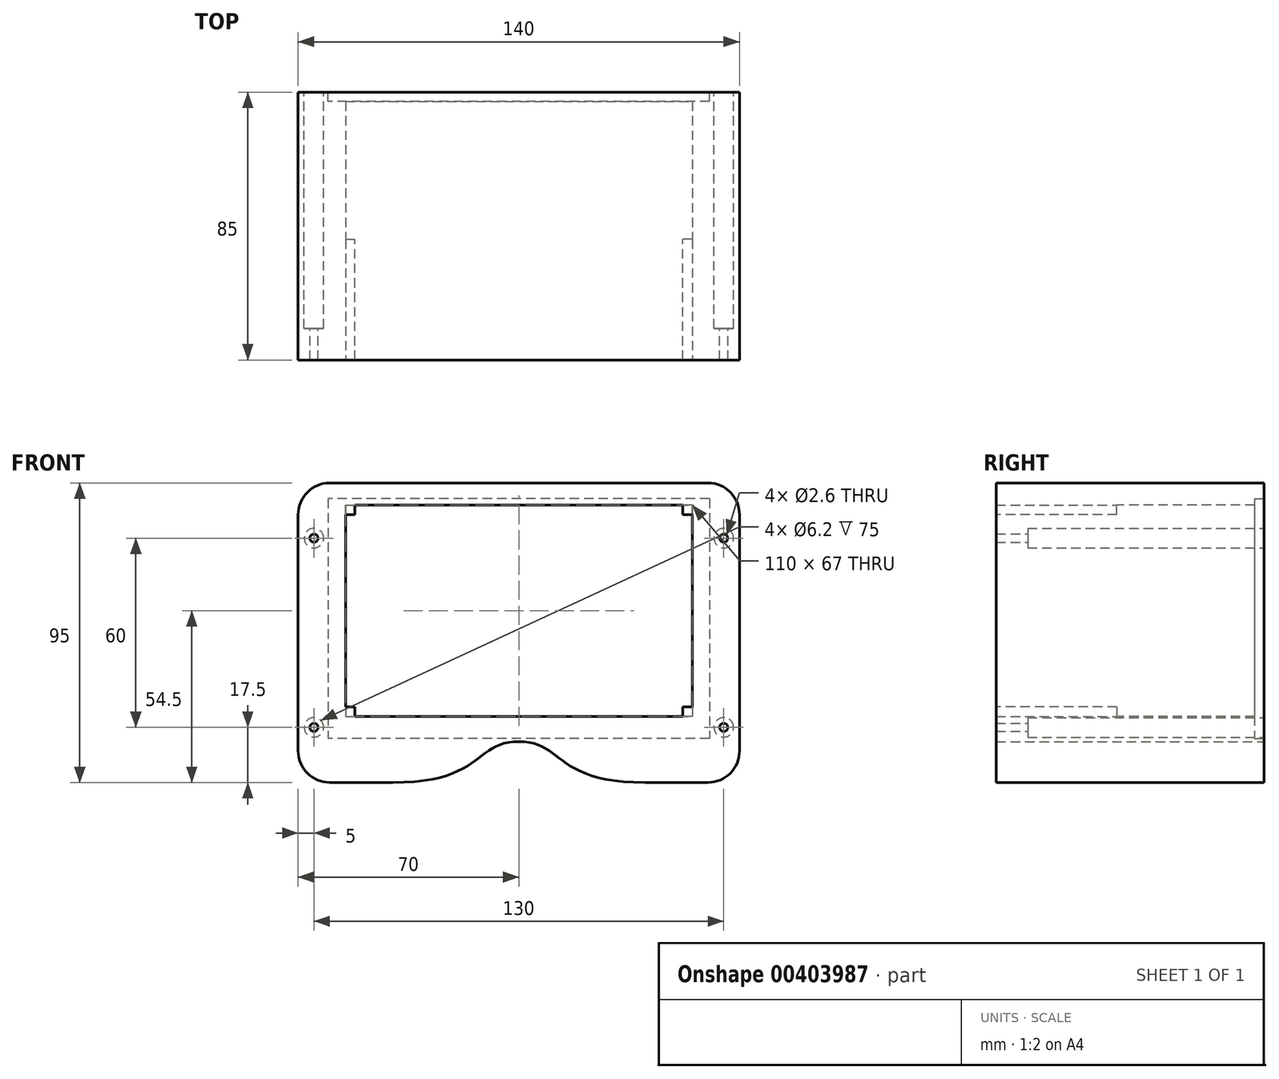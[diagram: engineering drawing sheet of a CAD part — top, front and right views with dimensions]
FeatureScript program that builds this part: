
annotation { "Feature Type Name" : "Feature", "Feature Type Description" : "" }
export const myFeature = defineFeature(function(context is Context, id is Id, definition is map)
    precondition{}
    {
        {
            var Q0;
            Q0=qCreatedBy(makeId("Top.planeOp"),FACE);
            var sketch = newSketch(context, id + "F0", { "sketchPlane" : qUnion([Q0])});
            skLineSegment(sketch, "E0.bottom", {"start": v(70, 85) * mm, "end": v(-70, 85) * mm});
            skLineSegment(sketch, "E0.top", {"start": v(70, -85) * mm, "end": v(-70, -85) * mm});
            skLineSegment(sketch, "E0.left", {"start": v(70, 85) * mm, "end": v(70, -85) * mm});
            skLineSegment(sketch, "E0.right", {"start": v(-70, 85) * mm, "end": v(-70, -85) * mm});
            skPoint(sketch, "E0.middle", {"position": v(0, 0) * mm});
            skSolve(sketch);
        }
        {
            var Q0;
            Q0=qSketchRegion(id+"F0",true);
            extrude(context, id + "F1", {"entities" : qUnion([Q0]), "depth" : 95 * mm});
        }
        {
            var Q0;
            Q0=makeQuery(id+"F1.opExtrude","SWEPT_FACE",FACE,{"disambiguationData":[OSD([sQuery(id+"F0.wireOp",EDGE,"E0.top")])]});
            var sketch = newSketch(context, id + "F2", { "sketchPlane" : qUnion([Q0])});
            skLineSegment(sketch, "E1.bottom", {"start": v(-55, 88) * mm, "end": v(55, 88) * mm});
            skLineSegment(sketch, "E1.top", {"start": v(-55, 21) * mm, "end": v(55, 21) * mm});
            skLineSegment(sketch, "E1.left", {"start": v(-55, 88) * mm, "end": v(-55, 21) * mm});
            skLineSegment(sketch, "E1.right", {"start": v(55, 88) * mm, "end": v(55, 21) * mm});
            skSolve(sketch);
        }
        {
            var Q0;
            Q0=qSketchRegion(id+"F2",true);
            extrude(context, id + "F3", {"entities" : qUnion([Q0]), "operationType" : NewBodyOperationType.REMOVE, "endBound" : BoundingType.THROUGH_ALL, "oppositeDirection" : true, "depth" : 25 * mm});
        }
        {
            var Q0;
            Q0=makeQuery(id+"F1.opExtrude","CAP_FACE",FACE,{"disambiguationData":[OSD([sQuery(id+"F0.wireOp",EDGE,"E0.bottom"),sQuery(id+"F0.wireOp",EDGE,"E0.top"),sQuery(id+"F0.wireOp",EDGE,"E0.left"),sQuery(id+"F0.wireOp",EDGE,"E0.right")])],"isStart":true});
            var sketch = newSketch(context, id + "F4", { "sketchPlane" : qUnion([Q0])});
            skLineSegment(sketch, "E2", {"start": v(0, -85) * mm, "end": v(0, 85) * mm, "construction": true});
            skLineSegment(sketch, "E3.1.0.0", {"start": v(-10, -85) * mm, "end": v(-10, 85) * mm, "construction": true});
            skLineSegment(sketch, "E3.2.0.0", {"start": v(-20, -85) * mm, "end": v(-20, 85) * mm, "construction": true});
            skLineSegment(sketch, "E3.3.0.0", {"start": v(-30, -85) * mm, "end": v(-30, 85) * mm, "construction": true});
            skLineSegment(sketch, "E3.4.0.0", {"start": v(-40, -85) * mm, "end": v(-40, 85) * mm, "construction": true});
            skLineSegment(sketch, "E3.5.0.0", {"start": v(-50, -85) * mm, "end": v(-50, 85) * mm, "construction": true});
            skLineSegment(sketch, "E3.6.0.0", {"start": v(-60, -85) * mm, "end": v(-60, 85) * mm, "construction": true});
            skLineSegment(sketch, "E3.direction1", {"start": v(0, -85) * mm, "end": v(-10, -85) * mm, "construction": true});
            skLineSegment(sketch, "E4.1.0.0", {"start": v(10, -85) * mm, "end": v(10, 85) * mm, "construction": true});
            skLineSegment(sketch, "E4.2.0.0", {"start": v(20, -85) * mm, "end": v(20, 85) * mm, "construction": true});
            skLineSegment(sketch, "E4.3.0.0", {"start": v(30, -85) * mm, "end": v(30, 85) * mm, "construction": true});
            skLineSegment(sketch, "E4.4.0.0", {"start": v(40, -85) * mm, "end": v(40, 85) * mm, "construction": true});
            skLineSegment(sketch, "E4.5.0.0", {"start": v(50, -85) * mm, "end": v(50, 85) * mm, "construction": true});
            skLineSegment(sketch, "E4.6.0.0", {"start": v(60, -85) * mm, "end": v(60, 85) * mm, "construction": true});
            skLineSegment(sketch, "E4.direction1", {"start": v(0, -85) * mm, "end": v(10, -85) * mm, "construction": true});
            skLineSegment(sketch, "E5", {"start": v(70, 15) * mm, "end": v(-70, 15) * mm, "construction": true});
            skLineSegment(sketch, "E6.0.1.0", {"start": v(70, 25) * mm, "end": v(-70, 25) * mm, "construction": true});
            skLineSegment(sketch, "E6.0.2.0", {"start": v(70, 35) * mm, "end": v(-70, 35) * mm, "construction": true});
            skLineSegment(sketch, "E6.0.3.0", {"start": v(70, 45) * mm, "end": v(-70, 45) * mm, "construction": true});
            skLineSegment(sketch, "E6.0.4.0", {"start": v(70, 55) * mm, "end": v(-70, 55) * mm, "construction": true});
            skLineSegment(sketch, "E6.0.5.0", {"start": v(70, 65) * mm, "end": v(-70, 65) * mm, "construction": true});
            skLineSegment(sketch, "E6.0.6.0", {"start": v(70, 75) * mm, "end": v(-70, 75) * mm, "construction": true});
            skLineSegment(sketch, "E6.1.0.0", {"start": v(95, 15) * mm, "end": v(-45, 15) * mm, "construction": true});
            skLineSegment(sketch, "E6.1.1.0", {"start": v(95, 25) * mm, "end": v(-45, 25) * mm, "construction": true});
            skLineSegment(sketch, "E6.1.2.0", {"start": v(95, 35) * mm, "end": v(-45, 35) * mm, "construction": true});
            skLineSegment(sketch, "E6.1.3.0", {"start": v(95, 45) * mm, "end": v(-45, 45) * mm, "construction": true});
            skLineSegment(sketch, "E6.1.4.0", {"start": v(95, 55) * mm, "end": v(-45, 55) * mm, "construction": true});
            skLineSegment(sketch, "E6.1.5.0", {"start": v(95, 65) * mm, "end": v(-45, 65) * mm, "construction": true});
            skLineSegment(sketch, "E6.1.6.0", {"start": v(95, 75) * mm, "end": v(-45, 75) * mm, "construction": true});
            skLineSegment(sketch, "E6.2.0.0", {"start": v(120, 15) * mm, "end": v(-20, 15) * mm, "construction": true});
            skLineSegment(sketch, "E6.2.1.0", {"start": v(120, 25) * mm, "end": v(-20, 25) * mm, "construction": true});
            skLineSegment(sketch, "E6.2.2.0", {"start": v(120, 35) * mm, "end": v(-20, 35) * mm, "construction": true});
            skLineSegment(sketch, "E6.2.3.0", {"start": v(120, 45) * mm, "end": v(-20, 45) * mm, "construction": true});
            skLineSegment(sketch, "E6.2.4.0", {"start": v(120, 55) * mm, "end": v(-20, 55) * mm, "construction": true});
            skLineSegment(sketch, "E6.2.5.0", {"start": v(120, 65) * mm, "end": v(-20, 65) * mm, "construction": true});
            skLineSegment(sketch, "E6.2.6.0", {"start": v(120, 75) * mm, "end": v(-20, 75) * mm, "construction": true});
            skLineSegment(sketch, "E6.direction1", {"start": v(-70, 15) * mm, "end": v(-45, 15) * mm, "construction": true});
            skLineSegment(sketch, "E6.direction2", {"start": v(-70, 15) * mm, "end": v(-70, 25) * mm, "construction": true});
            skFitSpline(sketch, "E7", {"points": [v(0, 15) * mm, v(20, 45) * mm, v(31.85, 56.6) * mm, v(68.26, 85) * mm], "startDerivative": vector(65.7, 0) * mm, "endDerivative": vector(77.5, 177.86) * mm});
            skFitSpline(sketch, "E8.MirrorCS", {"points": [v(0, 15) * mm, v(-20, 45) * mm, v(-31.85, 56.6) * mm, v(-68.26, 85) * mm], "startDerivative": vector(-65.7, 0) * mm, "endDerivative": vector(-77.5, 177.86) * mm});
            skLineSegment(sketch, "E9", {"start": v(68.26, 85) * mm, "end": v(-68.26, 85) * mm});
            skSolve(sketch);
        }
        {
            var Q0;
            Q0=makeQuery(id+"F4.imprint","IMPRINT",FACE,{"disambiguationData":[TD([[makeQuery(id+"F4.imprint","IMPRINT",EDGE,{"derivedFrom":sQuery(id+"F4.wireOp",EDGE,"E7")}),1.0]])]});
            extrude(context, id + "F5", {"entities" : qUnion([Q0]), "operationType" : NewBodyOperationType.REMOVE, "oppositeDirection" : true, "depth" : 88 * mm});
        }
        {
            var Q0;
            Q0=makeQuery(id+"F1.opExtrude","CAP_FACE",FACE,{"disambiguationData":[OSD([sQuery(id+"F0.wireOp",EDGE,"E0.bottom"),sQuery(id+"F0.wireOp",EDGE,"E0.top"),sQuery(id+"F0.wireOp",EDGE,"E0.left"),sQuery(id+"F0.wireOp",EDGE,"E0.right")])],"isStart":false});
            var sketch = newSketch(context, id + "F6", { "sketchPlane" : qUnion([Q0])});
            skLineSegment(sketch, "E10", {"start": v(-70, -55) * mm, "end": v(70, -55) * mm, "construction": true});
            skLineSegment(sketch, "E11", {"start": v(68.3, -85) * mm, "end": v(68.3, -55) * mm, "construction": true});
            skLineSegment(sketch, "E12", {"start": v(-68.36, -85) * mm, "end": v(-68.36, -55) * mm, "construction": true});
            skLineSegment(sketch, "E13", {"start": v(0, -85) * mm, "end": v(0, -55) * mm, "construction": true});
            skFitSpline(sketch, "E14", {"points": [v(0, -55) * mm, v(-47.97, -64.27) * mm, v(-68.36, -85) * mm], "startDerivative": vector(-134.93, 0) * mm, "endDerivative": vector(-37.97, -66.04) * mm});
            skFitSpline(sketch, "E15.MirrorCS", {"points": [v(0, -55) * mm, v(47.97, -64.27) * mm, v(68.36, -85) * mm], "startDerivative": vector(134.93, 0) * mm, "endDerivative": vector(37.97, -66.04) * mm});
            skLineSegment(sketch, "E16", {"start": v(-68.36, -85) * mm, "end": v(68.36, -85) * mm});
            skSolve(sketch);
        }
        {
            var Q0;
            Q0=makeQuery(id+"F6.imprint","IMPRINT",FACE,{"disambiguationData":[TD([[makeQuery(id+"F6.imprint","IMPRINT",EDGE,{"derivedFrom":sQuery(id+"F6.wireOp",EDGE,"E14")}),1.0]])]});
            extrude(context, id + "F7", {"entities" : qUnion([Q0]), "operationType" : NewBodyOperationType.REMOVE, "endBound" : BoundingType.UP_TO_NEXT, "oppositeDirection" : true, "depth" : 25 * mm});
        }
        {
            var Q0;
            Q0=makeQuery(id+"F1.opExtrude","CAP_EDGE",EDGE,{"disambiguationData":[OSD([sQuery(id+"F0.wireOp",EDGE,"E0.left")])],"isStart":false});
            var Q1;
            Q1=makeQuery(id+"F1.opExtrude","CAP_EDGE",EDGE,{"disambiguationData":[OSD([sQuery(id+"F0.wireOp",EDGE,"E0.left")])],"isStart":true});
            var Q2;
            Q2=makeQuery(id+"F1.opExtrude","CAP_EDGE",EDGE,{"disambiguationData":[OSD([sQuery(id+"F0.wireOp",EDGE,"E0.right")])],"isStart":true});
            var Q3;
            Q3=makeQuery(id+"F1.opExtrude","CAP_EDGE",EDGE,{"disambiguationData":[OSD([sQuery(id+"F0.wireOp",EDGE,"E0.right")])],"isStart":false});
            fillet(context, id + "F8", {"entities" : qUnion([Q0, Q1, Q2, Q3]), "radius" : 10 * mm, "tangentPropagation" : true, "allowEdgeOverflow" : false});
        }
        {
            var Q0;
            Q0=makeQuery(id+"F1.opExtrude","SWEPT_FACE",FACE,{"disambiguationData":[OSD([sQuery(id+"F0.wireOp",EDGE,"E0.bottom")])]});
            var sketch = newSketch(context, id + "F9", { "sketchPlane" : qUnion([Q0])});
            skLineSegment(sketch, "E17", {"start": v(0, 21) * mm, "end": v(0, 0) * mm, "construction": true});
            skLineSegment(sketch, "E18", {"start": v(-70, 13) * mm, "end": v(70, 13) * mm, "construction": true});
            skLineSegment(sketch, "E19", {"start": v(-40, 21) * mm, "end": v(-40, 0) * mm, "construction": true});
            skFitSpline(sketch, "E20", {"points": [v(0, 13) * mm, v(-40, 0) * mm], "startDerivative": vector(-42.54, 0) * mm, "endDerivative": vector(-86.95, 0) * mm});
            skFitSpline(sketch, "E21.MirrorCS", {"points": [v(0, 13) * mm, v(40, 0) * mm], "startDerivative": vector(42.54, 0) * mm, "endDerivative": vector(86.95, 0) * mm});
            skLineSegment(sketch, "E22", {"start": v(40, 0) * mm, "end": v(-40, 0) * mm});
            skSolve(sketch);
        }
        {
            var Q0;
            Q0=makeQuery(id+"F9.imprint","IMPRINT",FACE,{"disambiguationData":[TD([[makeQuery(id+"F9.imprint","IMPRINT",EDGE,{"derivedFrom":sQuery(id+"F9.wireOp",EDGE,"E20")}),1.0]])]});
            extrude(context, id + "F10", {"entities" : qUnion([Q0]), "operationType" : NewBodyOperationType.REMOVE, "endBound" : BoundingType.THROUGH_ALL, "oppositeDirection" : true, "depth" : 25 * mm});
        }
        {
            var Q0;
            Q0=makeQuery(id+"F1.opExtrude","SWEPT_FACE",FACE,{"disambiguationData":[OSD([sQuery(id+"F0.wireOp",EDGE,"E0.bottom")])]});
            var sketch = newSketch(context, id + "F11", { "sketchPlane" : qUnion([Q0])});
            skLineSegment(sketch, "E23.bottom", {"start": v(-60.5, 90) * mm, "end": v(60.5, 90) * mm});
            skLineSegment(sketch, "E23.top", {"start": v(-60.5, 14) * mm, "end": v(60.5, 14) * mm});
            skLineSegment(sketch, "E23.left", {"start": v(-60.5, 90) * mm, "end": v(-60.5, 14) * mm});
            skLineSegment(sketch, "E23.right", {"start": v(60.5, 90) * mm, "end": v(60.5, 14) * mm});
            skSolve(sketch);
        }
        {
            var Q0;
            Q0=makeQuery(id+"F11.imprint","IMPRINT",FACE,{"disambiguationData":[TD([[makeQuery(id+"F11.imprint","IMPRINT",EDGE,{"derivedFrom":sQuery(id+"F11.wireOp",EDGE,"E23.bottom")}),-1.0]])]});
            extrude(context, id + "F12", {"entities" : qUnion([Q0]), "operationType" : NewBodyOperationType.REMOVE, "oppositeDirection" : true, "depth" : 3 * mm});
        }
        {
            var Q0;
            Q0=makeQuery(id+"F3.boolean.opBoolean","COPY",FACE,{"derivedFrom":makeQuery(id+"F3.opExtrude","SWEPT_FACE",FACE,{"disambiguationData":[OSD([sQuery(id+"F2.wireOp",EDGE,"E1.top")])]})});
            var sketch = newSketch(context, id + "F13", { "sketchPlane" : qUnion([Q0])});
            skLineSegment(sketch, "E24.bottom", {"start": v(-55, -51.7) * mm, "end": v(-52, -51.7) * mm});
            skLineSegment(sketch, "E24.top", {"start": v(-55, 38.3) * mm, "end": v(-52, 38.3) * mm});
            skLineSegment(sketch, "E24.left", {"start": v(-55, -51.7) * mm, "end": v(-55, 38.3) * mm});
            skLineSegment(sketch, "E24.right", {"start": v(-52, -51.7) * mm, "end": v(-52, 38.3) * mm});
            skLineSegment(sketch, "E25.bottom", {"start": v(55, -51.7) * mm, "end": v(52, -51.7) * mm});
            skLineSegment(sketch, "E25.top", {"start": v(55, 38.3) * mm, "end": v(52, 38.3) * mm});
            skLineSegment(sketch, "E25.left", {"start": v(55, -51.7) * mm, "end": v(55, 38.3) * mm});
            skLineSegment(sketch, "E25.right", {"start": v(52, -51.7) * mm, "end": v(52, 38.3) * mm});
            skSolve(sketch);
        }
        {
            var Q0;
            Q0=qSketchRegion(id+"F13",true);
            extrude(context, id + "F14", {"entities" : qUnion([Q0]), "operationType" : NewBodyOperationType.ADD, "depth" : 3 * mm});
        }
        {
            var Q0;
            Q0=makeQuery(id+"F5.boolean.opBoolean","MERGE",FACE,{"derivedFrom":[makeQuery(id+"F3.boolean.opBoolean","COPY",FACE,{"derivedFrom":makeQuery(id+"F3.opExtrude","SWEPT_FACE",FACE,{"disambiguationData":[OSD([sQuery(id+"F2.wireOp",EDGE,"E1.bottom")])]})}),makeQuery(id+"F5.opExtrude","CAP_FACE",FACE,{"disambiguationData":[OSD([sQuery(id+"F4.wireOp",EDGE,"E7"),sQuery(id+"F4.wireOp",EDGE,"E8.MirrorCS"),sQuery(id+"F4.wireOp",EDGE,"E9")])],"isStart":false})]});
            var sketch = newSketch(context, id + "F15", { "sketchPlane" : qUnion([Q0])});
            skLineSegment(sketch, "E26.bottom", {"start": v(55, 51.7) * mm, "end": v(52, 51.7) * mm});
            skLineSegment(sketch, "E26.top", {"start": v(55, -38.3) * mm, "end": v(52, -38.3) * mm});
            skLineSegment(sketch, "E26.left", {"start": v(55, 51.7) * mm, "end": v(55, -38.3) * mm});
            skLineSegment(sketch, "E26.right", {"start": v(52, 51.7) * mm, "end": v(52, -38.3) * mm});
            skLineSegment(sketch, "E27.bottom", {"start": v(-55, 51.7) * mm, "end": v(-52, 51.7) * mm});
            skLineSegment(sketch, "E27.top", {"start": v(-55, -38.3) * mm, "end": v(-52, -38.3) * mm});
            skLineSegment(sketch, "E27.left", {"start": v(-55, 51.7) * mm, "end": v(-55, -38.3) * mm});
            skLineSegment(sketch, "E27.right", {"start": v(-52, 51.7) * mm, "end": v(-52, -38.3) * mm});
            skSolve(sketch);
        }
        {
            var Q0;
            Q0=qSketchRegion(id+"F15",true);
            extrude(context, id + "F16", {"entities" : qUnion([Q0]), "operationType" : NewBodyOperationType.ADD, "depth" : 3 * mm});
        }
        {
            var Q0;
            Q0=makeQuery(id+"F1.opExtrude","SWEPT_FACE",FACE,{"disambiguationData":[OSD([sQuery(id+"F0.wireOp",EDGE,"E0.bottom")])]});
            var sketch = newSketch(context, id + "F17", { "sketchPlane" : qUnion([Q0])});
            skLineSegment(sketch, "E28", {"start": v(-70, 47.5) * mm, "end": v(70, 47.5) * mm, "construction": true});
            skCircle(sketch, "E29", {"center": v(65, 77.5) * mm, "radius": 1.3 * mm});
            skLineSegment(sketch, "E30", {"start": v(0, 95) * mm, "end": v(0, 13) * mm, "construction": true});
            skCircle(sketch, "E31.MirrorC", {"center": v(65, 17.5) * mm, "radius": 1.3 * mm});
            skCircle(sketch, "E32.MirrorC", {"center": v(-65, 77.5) * mm, "radius": 1.3 * mm});
            skCircle(sketch, "E33.MirrorC", {"center": v(-65, 17.5) * mm, "radius": 1.3 * mm});
            skSolve(sketch);
        }
        {
            var Q0;
            Q0=qSketchRegion(id+"F17",true);
            extrude(context, id + "F18", {"entities" : qUnion([Q0]), "operationType" : NewBodyOperationType.REMOVE, "oppositeDirection" : true, "depth" : 100 * mm});
        }
        {
            var Q0;
            Q0=makeQuery(id+"F17.imprint","IMPRINT",FACE,{"disambiguationData":[TD([[makeQuery(id+"F17.imprint","IMPRINT",EDGE,{"derivedFrom":sQuery(id+"F17.wireOp",EDGE,"E29")}),-1.0]])]});
            var sketch = newSketch(context, id + "F19", { "sketchPlane" : qUnion([Q0])});
            skCircle(sketch, "E34", {"center": v(65, 77.5) * mm, "radius": 3.1 * mm});
            skCircle(sketch, "E35.MirrorC", {"center": v(65, 17.5) * mm, "radius": 3.1 * mm});
            skCircle(sketch, "E36.MirrorC", {"center": v(-65, 77.5) * mm, "radius": 3.1 * mm});
            skCircle(sketch, "E37.MirrorC", {"center": v(-65, 17.5) * mm, "radius": 3.1 * mm});
            skSolve(sketch);
        }
        {
            var Q0;
            Q0=qSketchRegion(id+"F19",true);
            extrude(context, id + "F20", {"entities" : qUnion([Q0]), "operationType" : NewBodyOperationType.REMOVE, "oppositeDirection" : true, "depth" : 75 * mm});
        }
        {
            var Q0;
            {var subQ2=sQuery(id+"F6.wireOp",EDGE,"E14");Q0=makeQuery(id+"F6.imprint","IMPRINT",FACE,{"disambiguationData":[TD([[makeQuery(id+"F6.imprint","IMPRINT",EDGE,{"derivedFrom":subQ2}),-1.0]])]});}
            var sketch = newSketch(context, id + "F21", { "sketchPlane" : qUnion([Q0])});
            skLineSegment(sketch, "E38.bottom", {"start": v(-72.6, 0) * mm, "end": v(72.4, 0) * mm});
            skLineSegment(sketch, "E39.top", {"start": v(-72.6, -89.2) * mm, "end": v(72.4, -89.2) * mm});
            skLineSegment(sketch, "E39.left", {"start": v(-72.6, 0) * mm, "end": v(-72.6, -89.2) * mm});
            skLineSegment(sketch, "E39.right", {"start": v(72.4, 0) * mm, "end": v(72.4, -89.2) * mm});
            skSolve(sketch);
        }
        {
            var Q0;
            Q0 = qSketchRegion(id + "F21", true);
            extrude(context, id + "F22", {"entities" : qUnion([Q0]), "operationType" : NewBodyOperationType.REMOVE, "endBound" : BoundingType.THROUGH_ALL, "oppositeDirection" : true, "depth" : 25 * mm});
        }
    });
